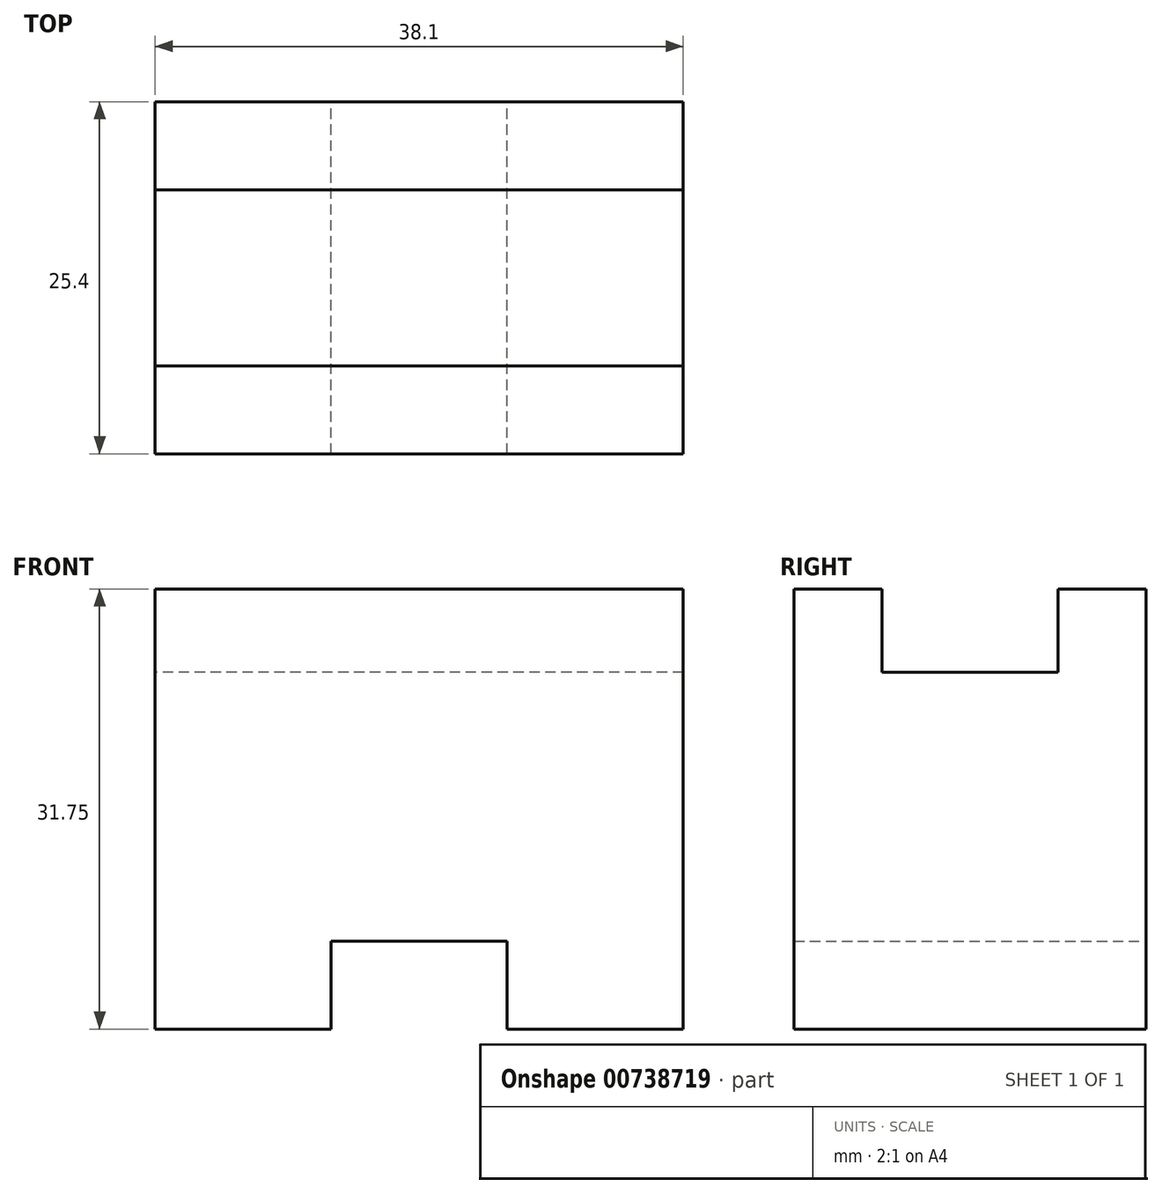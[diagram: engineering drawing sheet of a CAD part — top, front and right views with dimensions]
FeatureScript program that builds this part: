
annotation { "Feature Type Name" : "Feature", "Feature Type Description" : "" }
export const myFeature = defineFeature(function(context is Context, id is Id, definition is map)
    precondition{}
    {
        {
            var Q0;
            Q0=qCreatedBy(makeId("Front.planeOp"),FACE);
            var sketch = newSketch(context, id + "F0", { "sketchPlane" : qUnion([Q0])});
            skLineSegment(sketch, "E0", {"start": v(0, 31.75) * mm, "end": v(0, 0) * mm});
            skLineSegment(sketch, "E1", {"start": v(0, 0) * mm, "end": v(12.7, 0) * mm});
            skLineSegment(sketch, "E2", {"start": v(12.7, 0) * mm, "end": v(12.7, 6.35) * mm});
            skLineSegment(sketch, "E3", {"start": v(12.7, 6.35) * mm, "end": v(25.4, 6.35) * mm});
            skLineSegment(sketch, "E4", {"start": v(25.4, 6.35) * mm, "end": v(25.4, 0) * mm});
            skLineSegment(sketch, "E5", {"start": v(25.4, 0) * mm, "end": v(38.1, 0) * mm});
            skLineSegment(sketch, "E6", {"start": v(38.1, 0) * mm, "end": v(38.1, 31.75) * mm});
            skLineSegment(sketch, "E7", {"start": v(38.1, 31.75) * mm, "end": v(0, 31.75) * mm});
            skSolve(sketch);
        }
        {
            var Q0;
            Q0 = qSketchRegion(id + "F0", true);
            extrude(context, id + "F1", {"entities" : qUnion([Q0]), "depth" : 25.4 * mm, "offsetDistance" : 25.4 * mm});
        }
        {
            var Q0;
            Q0=qCreatedBy(makeId("Right.planeOp"),FACE);
            var sketch = newSketch(context, id + "F2", { "sketchPlane" : qUnion([Q0])});
            skLineSegment(sketch, "E8", {"start": v(-19.05, 32.09) * mm, "end": v(-19.05, 25.74) * mm});
            skLineSegment(sketch, "E9", {"start": v(-19.05, 25.74) * mm, "end": v(-6.35, 25.74) * mm});
            skLineSegment(sketch, "E10", {"start": v(-6.35, 25.74) * mm, "end": v(-6.35, 32.09) * mm});
            skLineSegment(sketch, "E11", {"start": v(-6.35, 32.09) * mm, "end": v(-19.05, 32.09) * mm});
            skSolve(sketch);
        }
        {
            var Q0;
            Q0 = qSketchRegion(id + "F2", true);
            extrude(context, id + "F3", {"entities" : qUnion([Q0]), "operationType" : NewBodyOperationType.REMOVE, "endBound" : BoundingType.THROUGH_ALL, "depth" : 25.4 * mm, "offsetDistance" : 25.4 * mm});
        }
    });
